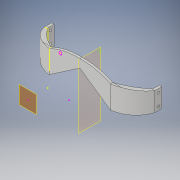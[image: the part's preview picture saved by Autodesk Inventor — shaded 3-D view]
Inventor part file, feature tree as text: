
AUTODESK INVENTOR PART (.ipt)
format: ipt  version: 2019 (Build 230136000, 136)  size: 206,336 bytes
history: native  units: mm
features: sketch x12, extrude x8, other x7, projected_geometry x3, mirror x2, loft x1
ambient origin geometry x8: Origin, YZ Plane, XZ Plane, XY Plane, X Axis, Y Axis, Z Axis, Center Point
bodies: Body1 (feature_tree)
feature tree (33):
  other  "Bryła1"
  sketch  "Szkic1"
  other  "Płaszczyzna konstrukcyjna8"
  sketch  "Szkic2"
  other  "Płaszczyzna konstrukcyjna2"
  extrude  "Wyciągnięcie proste1"  Depth=4.0mm
  sketch  "Szkic4"
  sketch  "Szkic5"
  other  "Płaszczyzna konstrukcyjna9"
  extrude  "Wyciągnięcie proste2"  Depth=8.9mm TaperAngle=0.0deg
  sketch  "Szkic20"
  sketch  "Szkic21"
  extrude  "Wyciągnięcie proste3"  Depth=3.0mm
  other  "Płaszczyzna konstrukcyjna10"
  extrude  "Wyciągnięcie proste4"  Depth=3.0mm
  extrude  "Wyciągnięcie proste5"  Depth=24.0mm
  extrude  "Wyciągnięcie proste6"  Depth=3.0mm TaperAngle=0.0deg
  loft  "Wyciągnięcie złożone2"
  extrude  "Wyciągnięcie proste7"  Depth=100.0mm TaperAngle=0.0deg
  mirror  "Odbij1"
  extrude  "Wyciągnięcie proste9"  Depth=250.0mm TaperAngle=0.0deg
  mirror  "Odbij2"
  sketch  "Szkic3"
  projected_geometry  "Pętla rzutowana1"
  projected_geometry  "Pętla rzutowana2"
  sketch  "Szkic19"
  projected_geometry  "Pętla rzutowana3"
  sketch  "Szkic23"
  sketch  "Szkic24"
  sketch  "Szkic25"
  other  "Krawędzie3"
  other  "Krawędzie4"
  sketch  "Szkic26"
